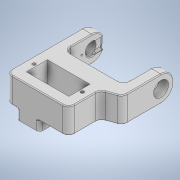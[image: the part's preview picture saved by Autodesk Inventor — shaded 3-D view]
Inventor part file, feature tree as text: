
AUTODESK INVENTOR PART (.ipt)
format: ipt  version: 2020.3 (Build 243373000, 373)  size: 457,216 bytes
history: native  units: mm
features: sketch x8, other x3, plane x1
ambient origin geometry x8: Origin, YZ Plane, XZ Plane, XY Plane, X Axis, Y Axis, Z Axis, Center Point
bodies: Solid1 (feature_tree)
feature tree (12):
  other  "LegStart_v1.ipt"
  other  "Solid1::LegStart_v1.ipt"
  other  "TaggingFeature1"
  sketch  "Sketch1"  dims[d0=10.0mm]
  sketch  "Sketch2"
  sketch  "Sketch3"
  sketch  "Sketch8"
  sketch  "Sketch9"
  sketch  "Sketch10"
  sketch  "Sketch11"
  sketch  "Sketch12"
  plane  "Work Plane1"
